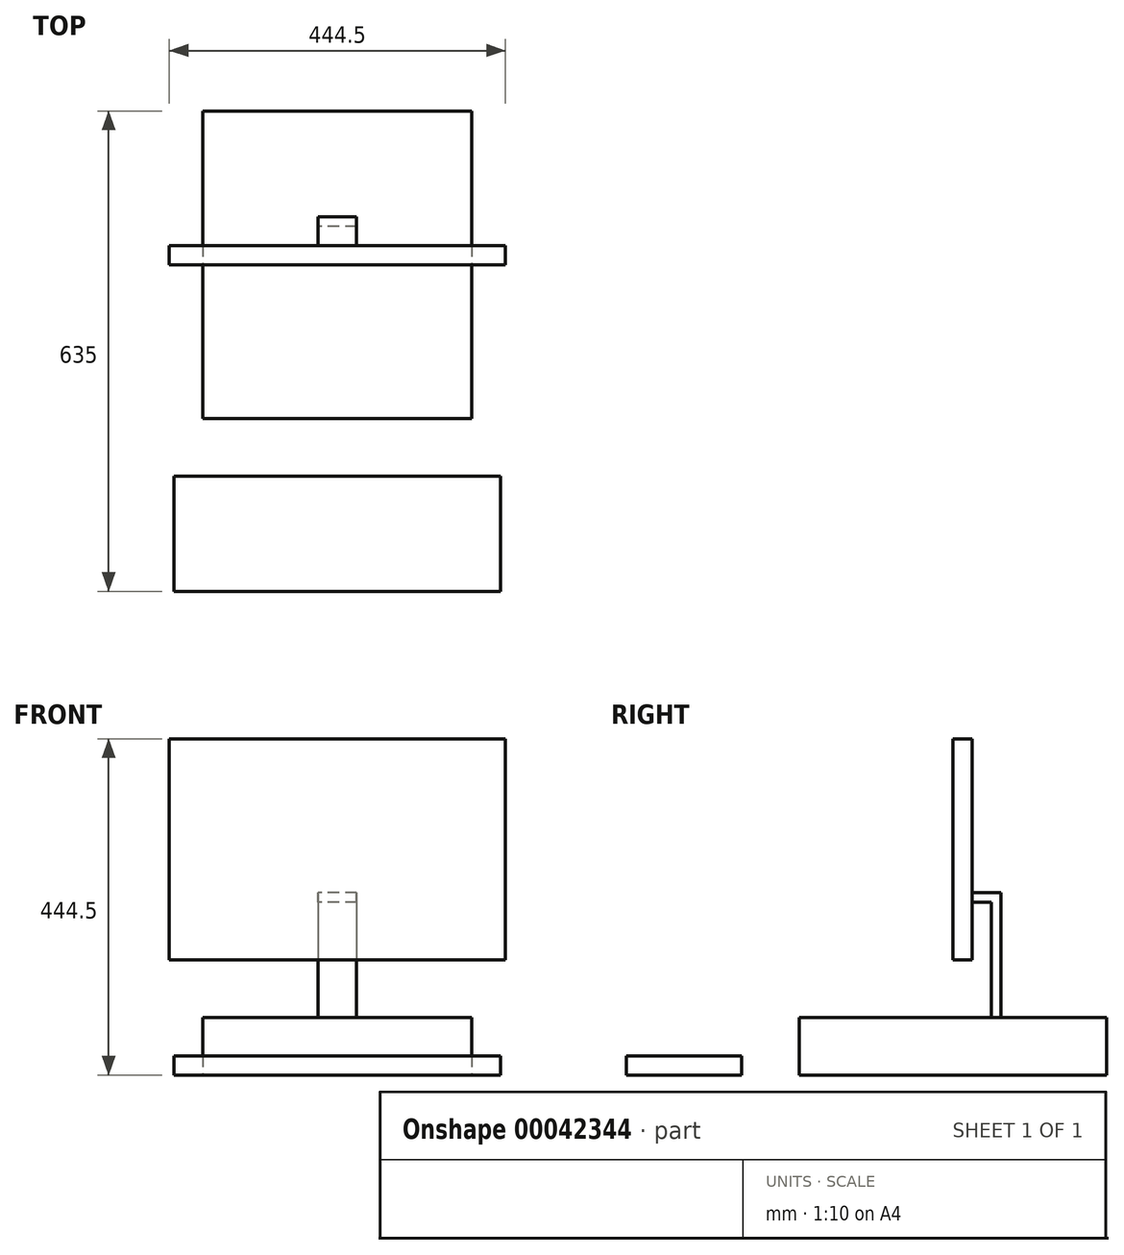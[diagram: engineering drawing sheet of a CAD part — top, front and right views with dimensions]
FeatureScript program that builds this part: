
annotation { "Feature Type Name" : "Feature", "Feature Type Description" : "" }
export const myFeature = defineFeature(function(context is Context, id is Id, definition is map)
    precondition{}
    {
        {
            var Q0;
            Q0=qCreatedBy(makeId("Top.planeOp"),FACE);
            var sketch = newSketch(context, id + "F0", { "sketchPlane" : qUnion([Q0])});
            skLineSegment(sketch, "E0.rect.bottom", {"start": v(177.8, 203.2) * mm, "end": v(-177.8, 203.2) * mm});
            skLineSegment(sketch, "E0.rect.top", {"start": v(177.8, -203.2) * mm, "end": v(-177.8, -203.2) * mm});
            skLineSegment(sketch, "E0.rect.left", {"start": v(177.8, 203.2) * mm, "end": v(177.8, -203.2) * mm});
            skLineSegment(sketch, "E0.rect.right", {"start": v(-177.8, 203.2) * mm, "end": v(-177.8, -203.2) * mm});
            skPoint(sketch, "E0.rect.middle", {"position": v(0, 0) * mm});
            skSolve(sketch);
        }
        {
            var Q0;
            Q0=qSketchRegion(id+"F0",true);
            extrude(context, id + "F1", {"entities" : qUnion([Q0]), "depth" : 76.2 * mm});
        }
        {
            var Q0;
            Q0=qCreatedBy(makeId("Right.planeOp"),FACE);
            var sketch = newSketch(context, id + "F2", { "sketchPlane" : qUnion([Q0])});
            skLineSegment(sketch, "E1", {"start": v(25.4, 241.3) * mm, "end": v(63.5, 241.3) * mm});
            skLineSegment(sketch, "E2", {"start": v(63.5, 241.3) * mm, "end": v(63.5, 76.2) * mm});
            skLineSegment(sketch, "E3", {"start": v(25.4, 228.6) * mm, "end": v(50.8, 228.6) * mm});
            skLineSegment(sketch, "E4", {"start": v(50.8, 228.6) * mm, "end": v(50.8, 76.2) * mm});
            skLineSegment(sketch, "E5", {"start": v(50.8, 76.2) * mm, "end": v(63.5, 76.2) * mm});
            skLineSegment(sketch, "E6", {"start": v(25.4, 228.6) * mm, "end": v(25.4, 241.3) * mm});
            skSolve(sketch);
        }
        {
            var Q0;
            Q0=makeQuery(id+"F2.imprint","IMPRINT",FACE,{"disambiguationData":[TD([[makeQuery(id+"F2.imprint","IMPRINT",EDGE,{"derivedFrom":sQuery(id+"F2.wireOp",EDGE,"E1")}),-1.0]])]});
            extrude(context, id + "F3", {"entities" : qUnion([Q0]), "operationType" : NewBodyOperationType.ADD, "endBound" : BoundingType.SYMMETRIC, "depth" : 50.8 * mm});
        }
        {
            var Q0;
            Q0=qCreatedBy(makeId("Front.planeOp"),FACE);
            var sketch = newSketch(context, id + "F4", { "sketchPlane" : qUnion([Q0])});
            skLineSegment(sketch, "E7.rect.top", {"start": v(222.25, 444.5) * mm, "end": v(-222.25, 444.5) * mm});
            skLineSegment(sketch, "E7.rect.left", {"start": v(222.25, 152.4) * mm, "end": v(222.25, 444.5) * mm});
            skLineSegment(sketch, "E7.rect.right", {"start": v(-222.25, 152.4) * mm, "end": v(-222.25, 444.5) * mm});
            skPoint(sketch, "E7.rect.middle", {"position": v(0, 298.45) * mm});
            skLineSegment(sketch, "E8", {"start": v(-222.25, 152.4) * mm, "end": v(222.25, 152.4) * mm});
            skSolve(sketch);
        }
        {
            var Q0;
            Q0=qSketchRegion(id+"F4",true);
            extrude(context, id + "F5", {"entities" : qUnion([Q0]), "operationType" : NewBodyOperationType.ADD, "oppositeDirection" : true, "depth" : 25.4 * mm});
        }
        {
            var Q0;
            Q0=makeQuery(id+"F1.opExtrude","CAP_FACE",FACE,{"disambiguationData":[OSD([sQuery(id+"F0.wireOp",EDGE,"E0.rect.bottom"),sQuery(id+"F0.wireOp",EDGE,"E0.rect.top"),sQuery(id+"F0.wireOp",EDGE,"E0.rect.left"),sQuery(id+"F0.wireOp",EDGE,"E0.rect.right")])],"isStart":true});
            cPlane(context, id + "F6", {"entities" : qUnion([Q0]), "cplaneType" : CPlaneType.OFFSET, "offset" : 0 * mm, "width" : 152.4 * mm, "height" : 152.4 * mm});
        }
        {
            var Q0;
            Q0=qCreatedBy(id+"F6.planeOp",FACE);
            var sketch = newSketch(context, id + "F7", { "sketchPlane" : qUnion([Q0])});
            skLineSegment(sketch, "E9.rect.bottom", {"start": v(215.9, 431.8) * mm, "end": v(-215.9, 431.8) * mm});
            skLineSegment(sketch, "E9.rect.top", {"start": v(215.9, 279.4) * mm, "end": v(-215.9, 279.4) * mm});
            skLineSegment(sketch, "E9.rect.left", {"start": v(215.9, 431.8) * mm, "end": v(215.9, 279.4) * mm});
            skLineSegment(sketch, "E9.rect.right", {"start": v(-215.9, 431.8) * mm, "end": v(-215.9, 279.4) * mm});
            skPoint(sketch, "E9.rect.middle", {"position": v(0, 355.6) * mm});
            skSolve(sketch);
        }
        {
            var Q0;
            Q0=makeQuery(id+"F7.imprint","IMPRINT",FACE,{"disambiguationData":[TD([[makeQuery(id+"F7.imprint","IMPRINT",EDGE,{"derivedFrom":sQuery(id+"F7.wireOp",EDGE,"E9.rect.bottom")}),1.0]])]});
            extrude(context, id + "F8", {"entities" : qUnion([Q0]), "oppositeDirection" : true, "depth" : 25.4 * mm});
        }
    });
